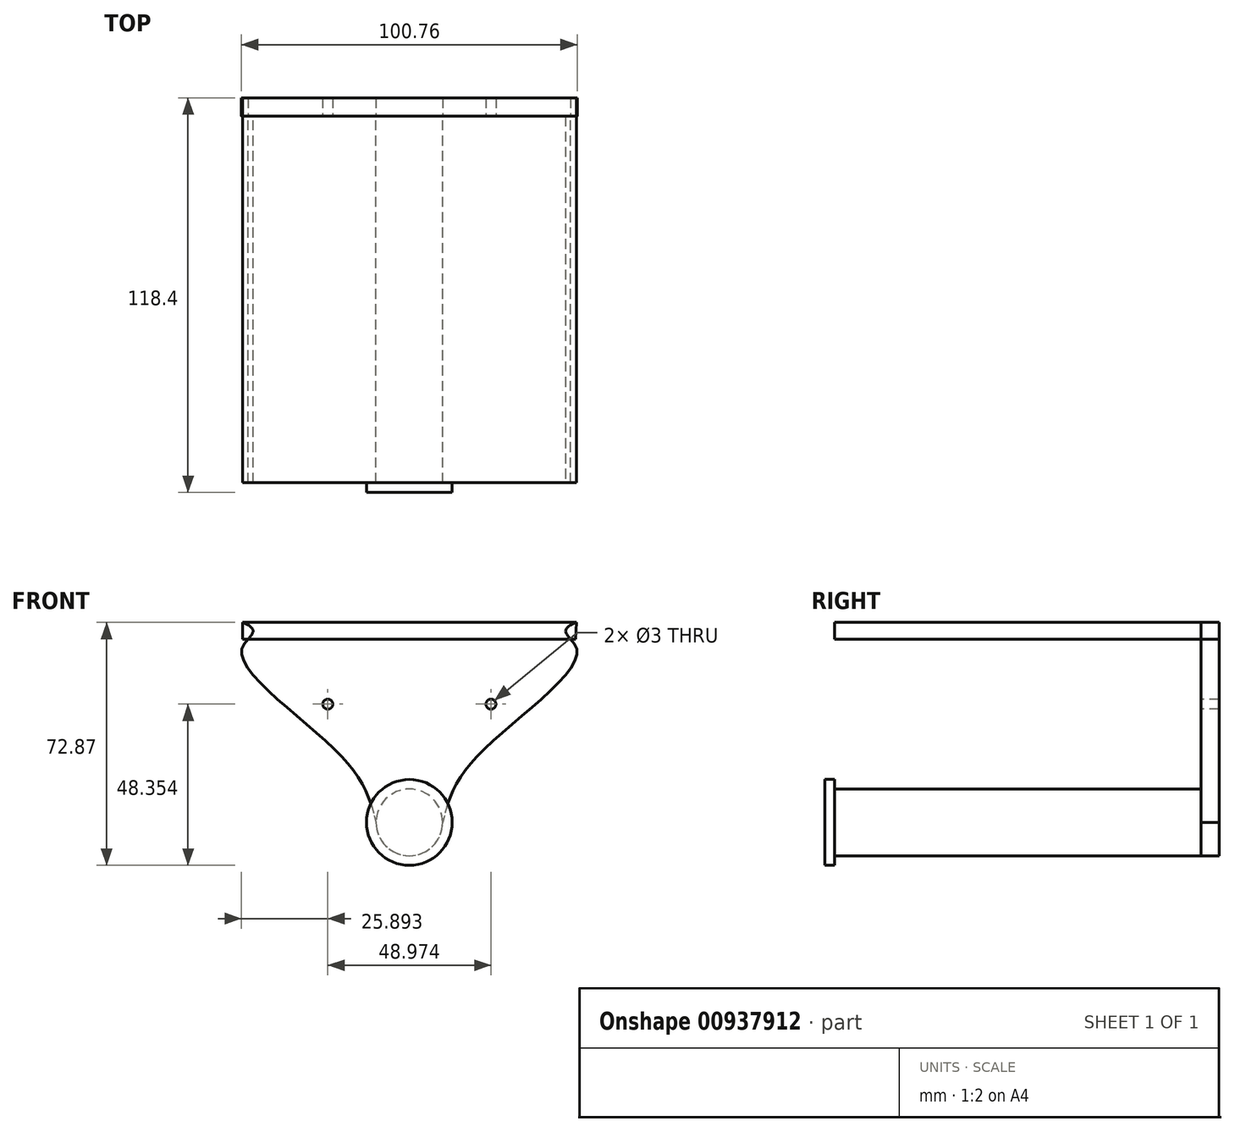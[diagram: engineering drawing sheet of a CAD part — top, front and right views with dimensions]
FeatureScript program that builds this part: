
annotation { "Feature Type Name" : "Feature", "Feature Type Description" : "" }
export const myFeature = defineFeature(function(context is Context, id is Id, definition is map)
    precondition{}
    {
        {
            var Q0;
            Q0=qCreatedBy(makeId("Front.planeOp"),FACE);
            var sketch = newSketch(context, id + "F0", { "sketchPlane" : qUnion([Q0])});
            skCircle(sketch, "E0", {"center": v(0, 0) * mm, "radius": 10 * mm});
            skLineSegment(sketch, "E1", {"start": v(0, 60) * mm, "end": v(-50.11, 60) * mm});
            skFitSpline(sketch, "E2", {"points": [v(-50.11, 60) * mm, v(-50.11, 52.62) * mm, v(-21.59, 21.14) * mm, v(-10, 0) * mm], "startDerivative": vector(102.5, -39.05) * mm, "endDerivative": vector(15.15, -62.38) * mm});
            skCircle(sketch, "E3", {"center": v(-24.49, 35.48) * mm, "radius": 1.5 * mm});
            skLineSegment(sketch, "E4.MirrorCS", {"start": v(0, 60) * mm, "end": v(50.11, 60) * mm});
            skFitSpline(sketch, "E5.MirrorCS", {"points": [v(50.11, 60) * mm, v(50.11, 52.62) * mm, v(21.59, 21.14) * mm, v(10, 0) * mm], "startDerivative": vector(-102.5, -39.05) * mm, "endDerivative": vector(-15.15, -62.38) * mm});
            skCircle(sketch, "E6.MirrorC", {"center": v(24.49, 35.48) * mm, "radius": 1.5 * mm});
            skLineSegment(sketch, "E7", {"start": v(-50.11, 55) * mm, "end": v(-50.11, 60) * mm});
            skLineSegment(sketch, "E8", {"start": v(-50.11, 55) * mm, "end": v(49.89, 55) * mm});
            skLineSegment(sketch, "E9", {"start": v(49.89, 55) * mm, "end": v(50.11, 60) * mm});
            skPoint(sketch, "E10", {"position": v(-50.11, 57.5) * mm});
            skSolve(sketch);
        }
        {
            var Q0;
            {var subQ2=sQuery(id+"F0.wireOp",EDGE,"E1");Q0=makeQuery(id+"F0.imprint","IMPRINT",FACE,{"disambiguationData":[TD([[makeQuery(id+"F0.imprint","IMPRINT",EDGE,{"derivedFrom":subQ2}),1.0]])]});}
            var Q1;
            {var subQ0=sQuery(id+"F0.wireOp",EDGE,"E0");var subQ1=makeQuery(id+"F0.imprint","INTERSECT",VERTEX,{"derivedFrom":[subQ0,sQuery(id+"F0.wireOp",EDGE,"E2")]});Q1=makeQuery(id+"F0.imprint","IMPRINT",FACE,{"disambiguationData":[TD([[makeQuery(id+"F0.imprint","IMPRINT",EDGE,{"disambiguationData":[TD([[subQ1,1.0]])],"derivedFrom":subQ0}),1.0]])]});}
            extrude(context, id + "F1", {"entities" : qUnion([Q0, Q1]), "depth" : 110 * mm, "offsetDistance" : 25 * mm});
        }
        {
            var Q0;
            Q0 = qSketchRegion(id + "F0", true);
            extrude(context, id + "F2", {"entities" : qUnion([Q0]), "oppositeDirection" : true, "depth" : 5.5 * mm, "offsetDistance" : 25 * mm});
        }
        {
            var Q0;
            Q0=makeQuery(id+"F1.opExtrude","CAP_FACE",FACE,{"disambiguationData":[OSD([sQuery(id+"F0.wireOp",EDGE,"E0")])],"isStart":false});
            var sketch = newSketch(context, id + "F3", { "sketchPlane" : qUnion([Q0])});
            skCircle(sketch, "E11", {"center": v(0, 0) * mm, "radius": 12.87 * mm});
            skSolve(sketch);
        }
        {
            var Q0;
            Q0=makeQuery(id+"F3.imprint","IMPRINT",FACE,{"disambiguationData":[TD([[makeQuery(id+"F3.imprint","IMPRINT",EDGE,{"derivedFrom":sQuery(id+"F3.wireOp",EDGE,"E11")}),1.0]])]});
            var Q1;
            Q1=makeQuery(id+"F3.imprint","IMPRINT",FACE,{"disambiguationData":[TD([[makeQuery(id+"F3.imprint","IMPRINT",EDGE,{"derivedFrom":makeQuery(id+"F1.opExtrude","CAP_EDGE",EDGE,{"disambiguationData":[OSD([sQuery(id+"F0.wireOp",EDGE,"E0")])],"isStart":false})}),1.0]])]});
            extrude(context, id + "F4", {"entities" : qUnion([Q0, Q1]), "operationType" : NewBodyOperationType.ADD, "depth" : 2.9 * mm, "offsetDistance" : 25 * mm});
        }
    });
